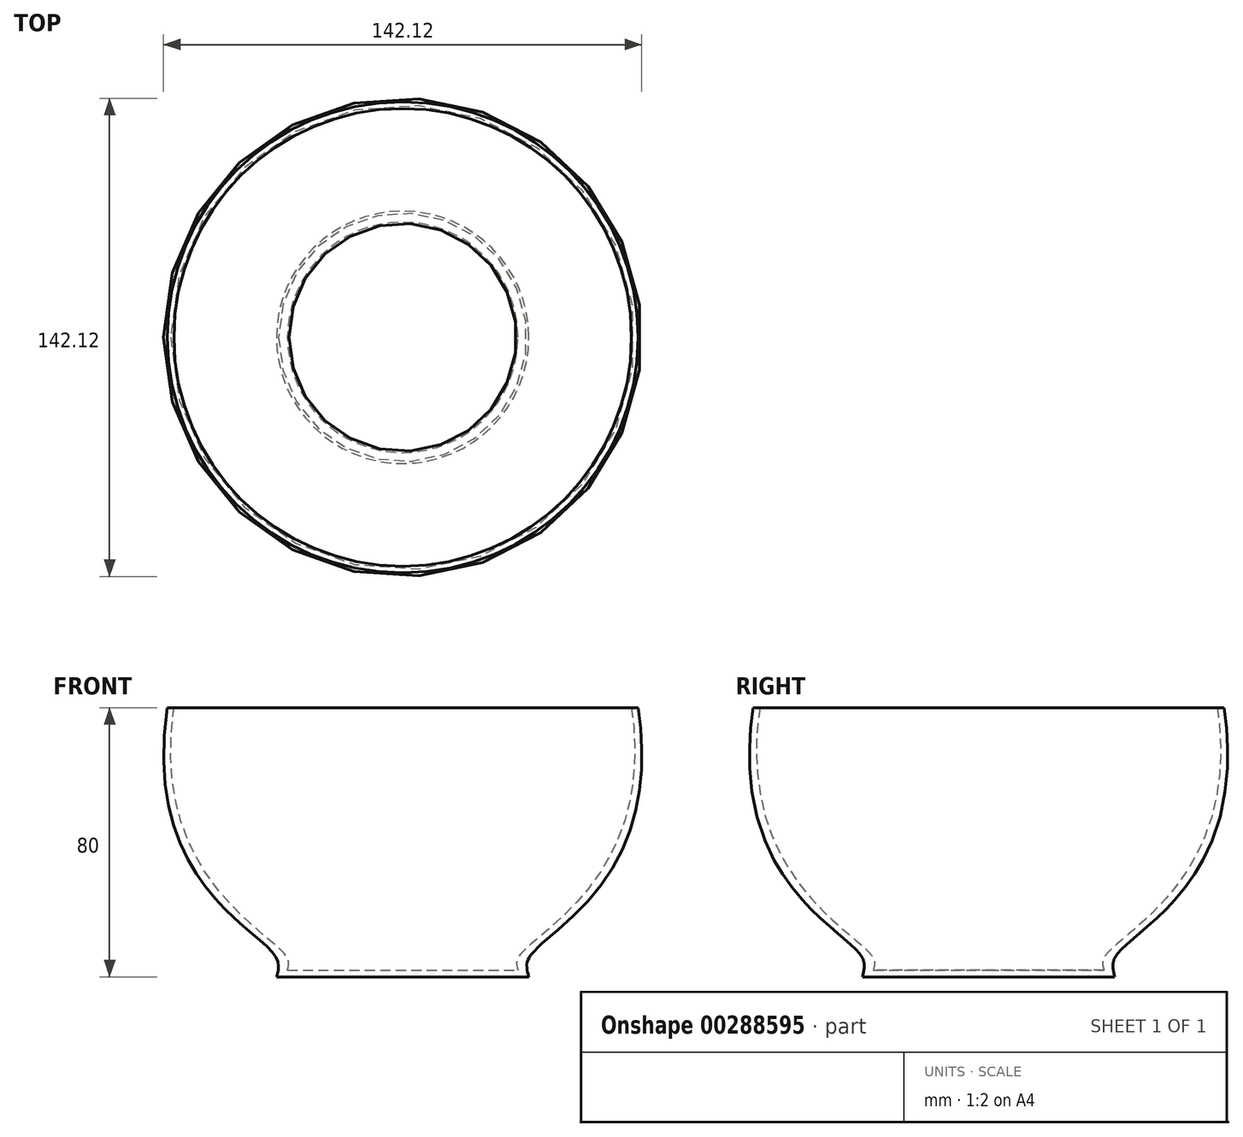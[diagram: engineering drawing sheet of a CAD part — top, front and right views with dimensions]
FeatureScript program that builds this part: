
annotation { "Feature Type Name" : "Feature", "Feature Type Description" : "" }
export const myFeature = defineFeature(function(context is Context, id is Id, definition is map)
    precondition{}
    {
        {
            var Q0;
            Q0=qCreatedBy(makeId("Front.planeOp"),FACE);
            var sketch = newSketch(context, id + "F0", { "sketchPlane" : qUnion([Q0])});
            skLineSegment(sketch, "E0", {"start": v(0, 0) * mm, "end": v(-37.5, 0) * mm});
            skFitSpline(sketch, "E1", {"points": [v(-37.5, 0) * mm, v(-37.5, 5.62) * mm, v(-70, 80) * mm], "startDerivative": vector(4.28, 20) * mm, "endDerivative": vector(28.8, 198) * mm});
            skLineSegment(sketch, "E2", {"start": v(-70, 80) * mm, "end": v(-68, 80) * mm});
            skLineSegment(sketch, "E3", {"start": v(0, 0) * mm, "end": v(0, 2) * mm});
            skLineSegment(sketch, "E4", {"start": v(0, 2) * mm, "end": v(-34.24, 2) * mm});
            skFitSpline(sketch, "E5", {"points": [v(-34.24, 2) * mm, v(-34.24, 5.62) * mm, v(-68, 80) * mm], "startDerivative": vector(3.55, 14.8) * mm, "endDerivative": vector(26.92, 184.96) * mm});
            skSolve(sketch);
        }
        {
            var Q0;
            Q0=makeQuery(id+"F0.imprint","IMPRINT",FACE,{"disambiguationData":[TD([[makeQuery(id+"F0.imprint","IMPRINT",EDGE,{"derivedFrom":sQuery(id+"F0.wireOp",EDGE,"E0")}),-1.0]])]});
            var Q1;
            Q1=sQuery(id+"F0.wireOp",EDGE,"E3");
            revolve(context, id + "F1", {"entities" : qUnion([Q0]), "axis" : qUnion([Q1]), "revolveType" : RevolveType.FULL});
        }
    });
